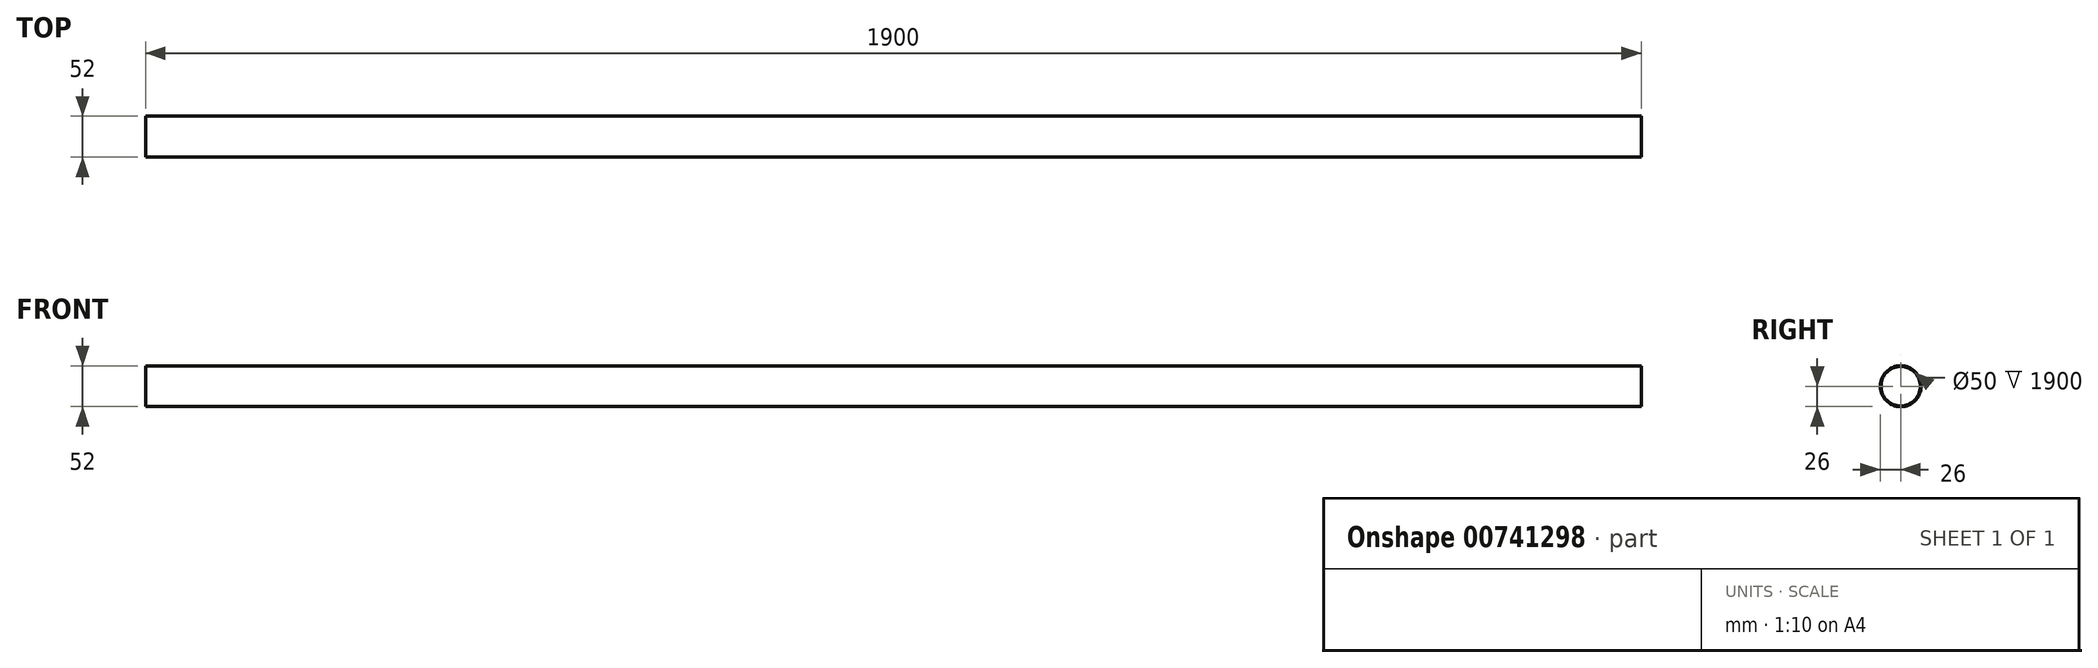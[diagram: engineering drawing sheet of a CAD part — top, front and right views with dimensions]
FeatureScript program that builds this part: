
annotation { "Feature Type Name" : "Feature", "Feature Type Description" : "" }
export const myFeature = defineFeature(function(context is Context, id is Id, definition is map)
    precondition{}
    {
        {
            var Q0;
            Q0=qCreatedBy(makeId("Right.planeOp"),FACE);
            var sketch = newSketch(context, id + "F0", { "sketchPlane" : qUnion([Q0])});
            skCircle(sketch, "E0", {"center": v(0, 0) * mm, "radius": 26 * mm});
            skCircle(sketch, "E1", {"center": v(0, 0) * mm, "radius": 25 * mm});
            skSolve(sketch);
        }
        {
            var Q0;
            Q0=qSketchRegion(id+"F0",true);
            extrude(context, id + "F1", {"entities" : qUnion([Q0]), "endBound" : BoundingType.SYMMETRIC, "depth" : 1900 * mm, "offsetDistance" : 25 * mm});
        }
    });
